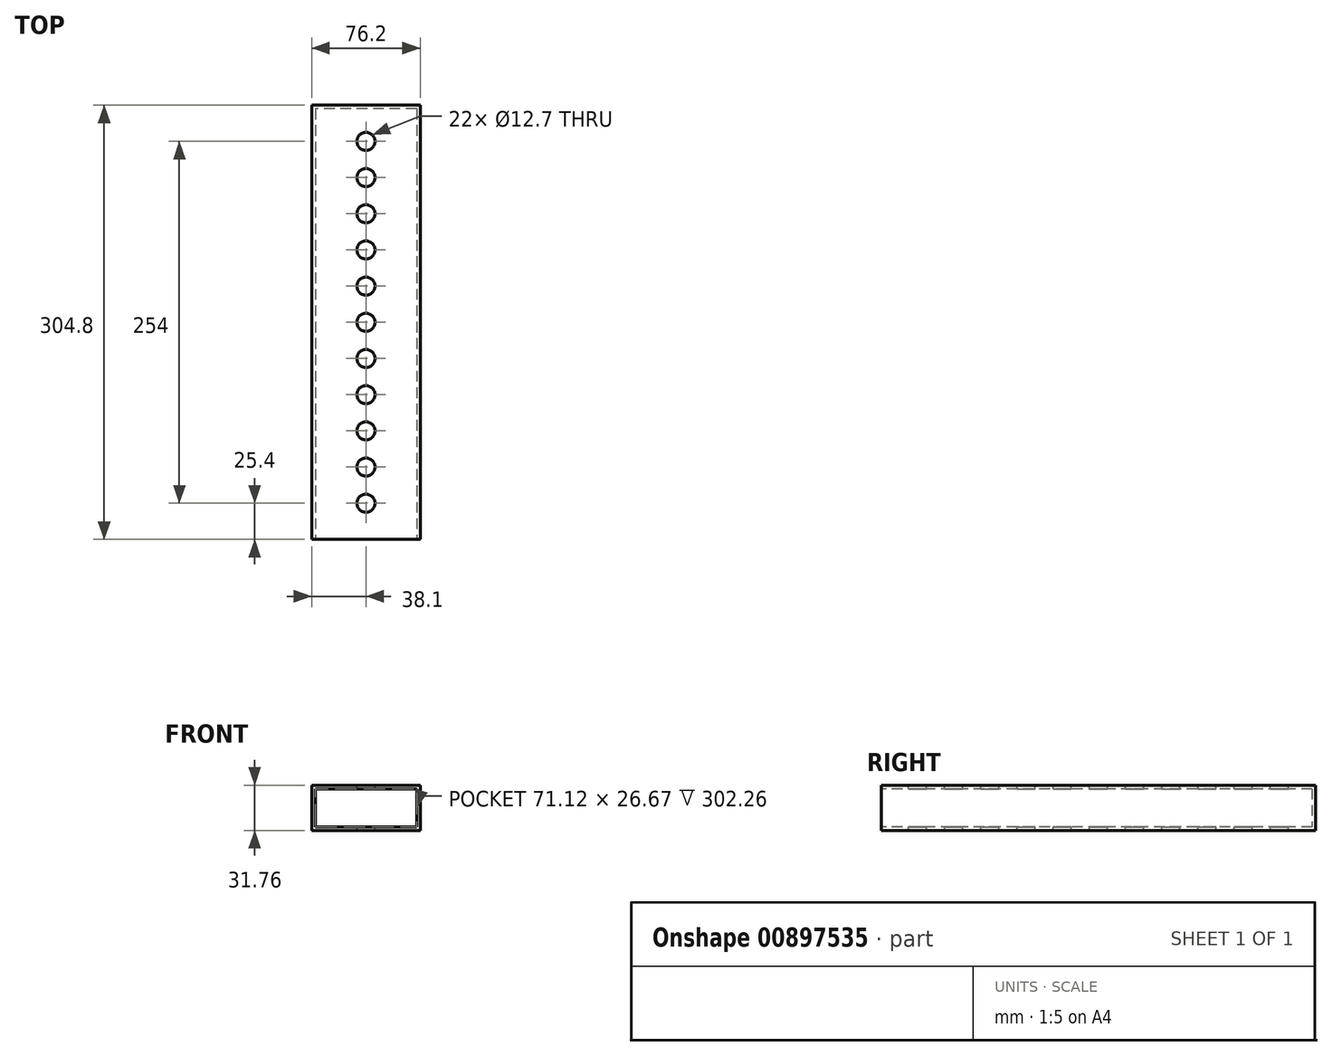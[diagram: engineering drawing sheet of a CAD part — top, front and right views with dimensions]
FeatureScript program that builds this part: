
annotation { "Feature Type Name" : "Feature", "Feature Type Description" : "" }
export const myFeature = defineFeature(function(context is Context, id is Id, definition is map)
    precondition{}
    {
        {
            var Q0;
            Q0=qCreatedBy(makeId("Front.planeOp"),FACE);
            var sketch = newSketch(context, id + "F0", { "sketchPlane" : qUnion([Q0])});
            skLineSegment(sketch, "E0.bottom", {"start": v(38.1, 15.88) * mm, "end": v(-38.1, 15.88) * mm});
            skLineSegment(sketch, "E0.top", {"start": v(38.1, -15.88) * mm, "end": v(-38.1, -15.88) * mm});
            skLineSegment(sketch, "E0.left", {"start": v(38.1, 15.88) * mm, "end": v(38.1, -15.87) * mm});
            skLineSegment(sketch, "E0.right", {"start": v(-38.1, 15.88) * mm, "end": v(-38.1, -15.88) * mm});
            skPoint(sketch, "E0.middle", {"position": v(0, 0) * mm});
            skSolve(sketch);
        }
        {
            var Q0;
            Q0=makeQuery(id+"F0.imprint","IMPRINT",FACE,{"disambiguationData":[TD([[makeQuery(id+"F0.imprint","IMPRINT",EDGE,{"derivedFrom":sQuery(id+"F0.wireOp",EDGE,"E0.bottom")}),1.0]])]});
            extrude(context, id + "F1", {"entities" : qUnion([Q0]), "oppositeDirection" : true, "depth" : 304.8 * mm, "offsetDistance" : 25.4 * mm});
        }
        {
            var Q0;
            Q0=makeQuery(id+"F1.opExtrude","CAP_FACE",FACE,{"disambiguationData":[OSD([sQuery(id+"F0.wireOp",EDGE,"E0.bottom"),sQuery(id+"F0.wireOp",EDGE,"E0.top"),sQuery(id+"F0.wireOp",EDGE,"E0.left"),sQuery(id+"F0.wireOp",EDGE,"E0.right")])],"isStart":true});
            shell(context, id + "F2", {"entities" : qUnion([Q0]), "thickness" : 2.54 * mm});
        }
        {
            var Q0;
            Q0=makeQuery(id+"F1.opExtrude","SWEPT_FACE",FACE,{"disambiguationData":[OSD([sQuery(id+"F0.wireOp",EDGE,"E0.bottom")])]});
            var sketch = newSketch(context, id + "F3", { "sketchPlane" : qUnion([Q0])});
            skPoint(sketch, "E1", {"position": v(0, 152.4) * mm});
            skPoint(sketch, "E2", {"position": v(0, 127) * mm});
            skPoint(sketch, "E3", {"position": v(0, 76.2) * mm});
            skPoint(sketch, "E4", {"position": v(0, 25.4) * mm});
            skPoint(sketch, "E5", {"position": v(0, 50.8) * mm});
            skPoint(sketch, "E6", {"position": v(0, 228.6) * mm});
            skPoint(sketch, "E7", {"position": v(0, 279.4) * mm});
            skPoint(sketch, "E8", {"position": v(0, 254) * mm});
            skPoint(sketch, "E9", {"position": v(0, 203.2) * mm});
            skPoint(sketch, "E10", {"position": v(0, 177.8) * mm});
            skPoint(sketch, "E11", {"position": v(0, 101.6) * mm});
            skSolve(sketch);
        }
        {
            var Q0;
            Q0=sQuery(id+"F3.wireOp",VERTEX,"E7");
            var Q1;
            Q1=sQuery(id+"F3.wireOp",VERTEX,"E8");
            var Q2;
            Q2=sQuery(id+"F3.wireOp",VERTEX,"E6");
            var Q3;
            Q3=sQuery(id+"F3.wireOp",VERTEX,"E9");
            var Q4;
            Q4=sQuery(id+"F3.wireOp",VERTEX,"E10");
            var Q5;
            Q5=sQuery(id+"F3.wireOp",VERTEX,"E1");
            var Q6;
            Q6=sQuery(id+"F3.wireOp",VERTEX,"E2");
            var Q7;
            Q7=sQuery(id+"F3.wireOp",VERTEX,"E11");
            var Q8;
            Q8=sQuery(id+"F3.wireOp",VERTEX,"E3");
            var Q9;
            Q9=sQuery(id+"F3.wireOp",VERTEX,"E4");
            var Q10;
            Q10=sQuery(id+"F3.wireOp",VERTEX,"E5");
            var Q11;
            Q11=makeQuery(id+"F1.opExtrude","SWEPT_BODY",BODY,{"disambiguationData":[OSD([sQuery(id+"F0.wireOp",EDGE,"E0.bottom"),sQuery(id+"F0.wireOp",EDGE,"E0.top"),sQuery(id+"F0.wireOp",EDGE,"E0.left"),sQuery(id+"F0.wireOp",EDGE,"E0.right")])]});
            hole(context, id + "F4", {"style" : HoleStyle.SIMPLE, "endStyle" : HoleEndStyle.THROUGH, "holeDiameter" : 12.7 * mm, "majorDiameter" : 6.35 * mm, "isTappedThrough" : true, "tappedDepth" : 12.7 * mm, "tapClearance" : 3, "locations" : qUnion([Q0, Q1, Q2, Q3, Q4, Q5, Q6, Q7, Q8, Q9, Q10]), "scope" : qUnion([Q11])});
        }
    });
